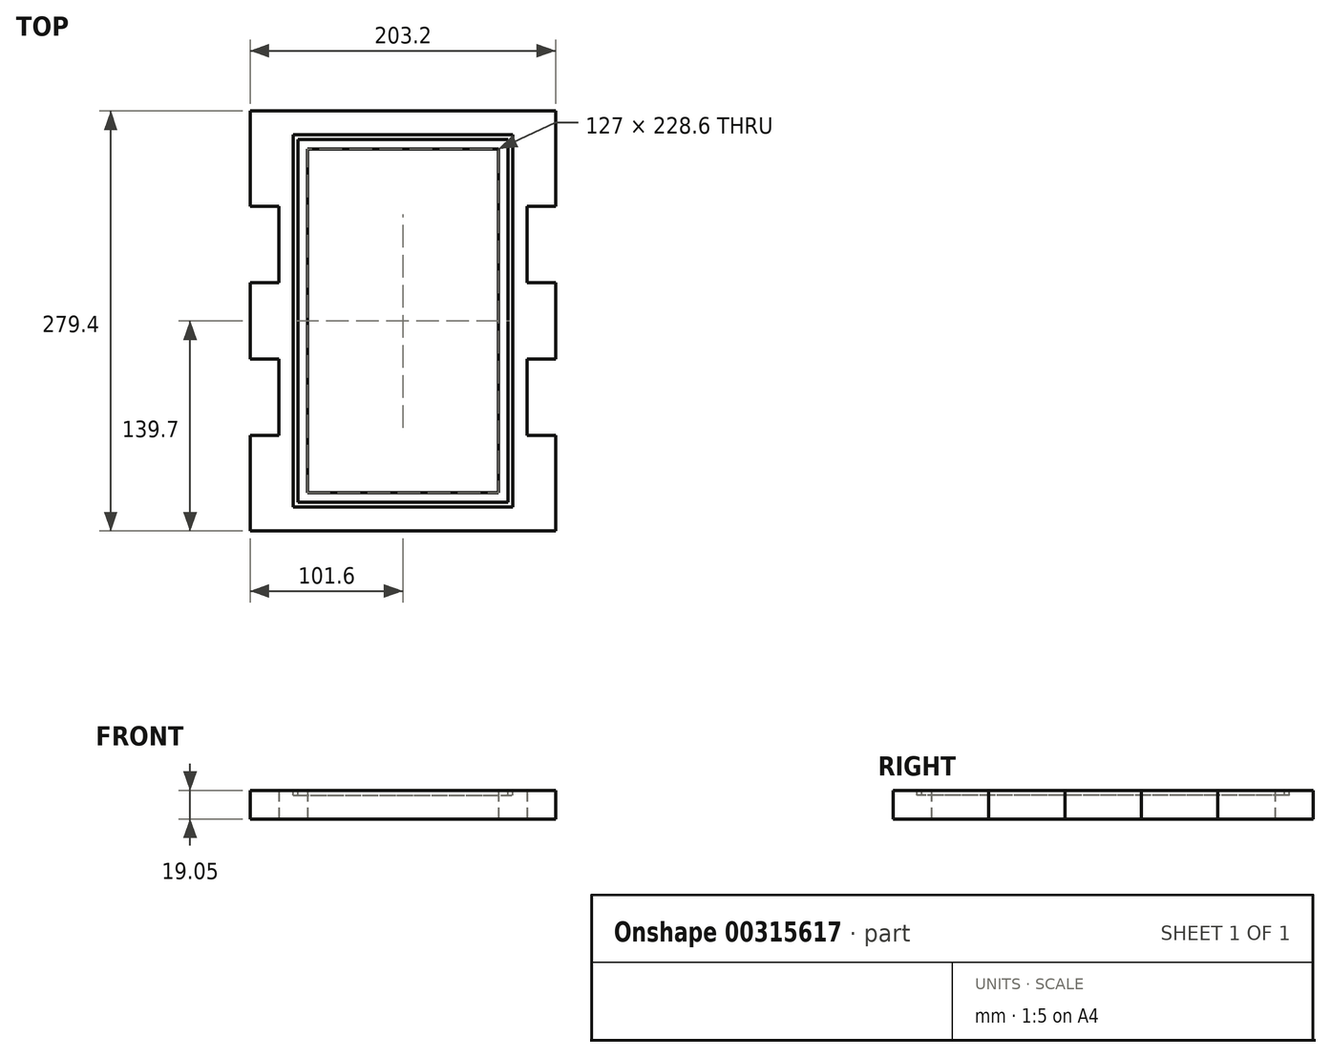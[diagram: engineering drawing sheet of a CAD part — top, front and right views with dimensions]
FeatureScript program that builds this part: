
annotation { "Feature Type Name" : "Feature", "Feature Type Description" : "" }
export const myFeature = defineFeature(function(context is Context, id is Id, definition is map)
    precondition{}
    {
        {
            var Q0;
            Q0=qCreatedBy(makeId("Top.planeOp"),FACE);
            var sketch = newSketch(context, id + "F0", { "sketchPlane" : qUnion([Q0])});
            skLineSegment(sketch, "E0.bottom", {"start": v(-101.6, 139.7) * mm, "end": v(101.6, 139.7) * mm});
            skLineSegment(sketch, "E0.top", {"start": v(-101.6, -139.7) * mm, "end": v(101.6, -139.7) * mm});
            skLineSegment(sketch, "E0.left", {"start": v(-101.6, 139.7) * mm, "end": v(-101.6, -139.7) * mm});
            skLineSegment(sketch, "E0.right", {"start": v(101.6, 139.7) * mm, "end": v(101.6, -139.7) * mm});
            skPoint(sketch, "E0.middle", {"position": v(0, 0) * mm});
            skLineSegment(sketch, "E1", {"start": v(-101.6, 76.2) * mm, "end": v(101.6, 76.2) * mm, "construction": true});
            skLineSegment(sketch, "E2", {"start": v(-101.6, -76.2) * mm, "end": v(101.6, -76.2) * mm, "construction": true});
            skLineSegment(sketch, "E3.bottom", {"start": v(-101.6, -76.2) * mm, "end": v(-82.55, -76.2) * mm});
            skLineSegment(sketch, "E3.top", {"start": v(-101.6, -25.4) * mm, "end": v(-82.55, -25.4) * mm});
            skLineSegment(sketch, "E3.left", {"start": v(-101.6, -76.2) * mm, "end": v(-101.6, -25.4) * mm});
            skLineSegment(sketch, "E3.right", {"start": v(-82.55, -76.2) * mm, "end": v(-82.55, -25.4) * mm});
            skLineSegment(sketch, "E4.bottom", {"start": v(-101.6, 76.2) * mm, "end": v(-82.55, 76.2) * mm});
            skLineSegment(sketch, "E4.top", {"start": v(-101.6, 25.4) * mm, "end": v(-82.55, 25.4) * mm});
            skLineSegment(sketch, "E4.left", {"start": v(-101.6, 76.2) * mm, "end": v(-101.6, 25.4) * mm});
            skLineSegment(sketch, "E4.right", {"start": v(-82.55, 76.2) * mm, "end": v(-82.55, 25.4) * mm});
            skLineSegment(sketch, "E5.bottom", {"start": v(101.6, 76.2) * mm, "end": v(82.55, 76.2) * mm});
            skLineSegment(sketch, "E5.top", {"start": v(101.6, 25.4) * mm, "end": v(82.55, 25.4) * mm});
            skLineSegment(sketch, "E5.left", {"start": v(101.6, 76.2) * mm, "end": v(101.6, 25.4) * mm});
            skLineSegment(sketch, "E5.right", {"start": v(82.55, 76.2) * mm, "end": v(82.55, 25.4) * mm});
            skLineSegment(sketch, "E6.bottom", {"start": v(101.6, -76.2) * mm, "end": v(82.55, -76.2) * mm});
            skLineSegment(sketch, "E6.top", {"start": v(101.6, -25.4) * mm, "end": v(82.55, -25.4) * mm});
            skLineSegment(sketch, "E6.left", {"start": v(101.6, -76.2) * mm, "end": v(101.6, -25.4) * mm});
            skLineSegment(sketch, "E6.right", {"start": v(82.55, -76.2) * mm, "end": v(82.55, -25.4) * mm});
            skLineSegment(sketch, "E7.bottom", {"start": v(-63.5, 114.3) * mm, "end": v(63.5, 114.3) * mm});
            skLineSegment(sketch, "E7.top", {"start": v(-63.5, -114.3) * mm, "end": v(63.5, -114.3) * mm});
            skLineSegment(sketch, "E7.left", {"start": v(-63.5, 114.3) * mm, "end": v(-63.5, -114.3) * mm});
            skLineSegment(sketch, "E7.right", {"start": v(63.5, 114.3) * mm, "end": v(63.5, -114.3) * mm});
            skSolve(sketch);
        }
        {
            var Q0;
            {var subQ10=sQuery(id+"F0.wireOp",EDGE,"E0.bottom");Q0=makeQuery(id+"F0.imprint","IMPRINT",FACE,{"disambiguationData":[TD([[makeQuery(id+"F0.imprint","IMPRINT",EDGE,{"derivedFrom":subQ10}),-1.0]])]});}
            extrude(context, id + "F1", {"entities" : qUnion([Q0]), "depth" : 19.05 * mm});
        }
        {
            var Q0;
            Q0=makeQuery(id+"F1.opExtrude","CAP_FACE",FACE,{"disambiguationData":[OSD([sQuery(id+"F0.wireOp",EDGE,"E0.bottom"),sQuery(id+"F0.wireOp",EDGE,"E0.top"),sQuery(id+"F0.wireOp",EDGE,"E0.left"),sQuery(id+"F0.wireOp",EDGE,"E0.right"),sQuery(id+"F0.wireOp",EDGE,"E3.bottom"),sQuery(id+"F0.wireOp",EDGE,"E3.top"),sQuery(id+"F0.wireOp",EDGE,"E3.right"),sQuery(id+"F0.wireOp",EDGE,"E4.bottom"),sQuery(id+"F0.wireOp",EDGE,"E4.top"),sQuery(id+"F0.wireOp",EDGE,"E4.right"),sQuery(id+"F0.wireOp",EDGE,"E5.bottom"),sQuery(id+"F0.wireOp",EDGE,"E5.top"),sQuery(id+"F0.wireOp",EDGE,"E5.right"),sQuery(id+"F0.wireOp",EDGE,"E6.bottom"),sQuery(id+"F0.wireOp",EDGE,"E6.top"),sQuery(id+"F0.wireOp",EDGE,"E6.right"),sQuery(id+"F0.wireOp",EDGE,"E7.bottom"),sQuery(id+"F0.wireOp",EDGE,"E7.top"),sQuery(id+"F0.wireOp",EDGE,"E7.left"),sQuery(id+"F0.wireOp",EDGE,"E7.right")])],"isStart":false});
            var sketch = newSketch(context, id + "F2", { "sketchPlane" : qUnion([Q0])});
            skLineSegment(sketch, "E8.bottom", {"start": v(-69.85, 120.65) * mm, "end": v(69.85, 120.65) * mm});
            skLineSegment(sketch, "E8.top", {"start": v(-69.85, -120.65) * mm, "end": v(69.85, -120.65) * mm});
            skLineSegment(sketch, "E8.left", {"start": v(-69.85, 120.65) * mm, "end": v(-69.85, -120.65) * mm});
            skLineSegment(sketch, "E8.right", {"start": v(69.85, 120.65) * mm, "end": v(69.85, -120.65) * mm});
            skPoint(sketch, "E8.middle", {"position": v(0, 0) * mm});
            skLineSegment(sketch, "E9.bottom", {"start": v(-73.02, 123.83) * mm, "end": v(73.02, 123.83) * mm});
            skLineSegment(sketch, "E9.top", {"start": v(-73.02, -123.83) * mm, "end": v(73.02, -123.83) * mm});
            skLineSegment(sketch, "E9.left", {"start": v(-73.03, 123.83) * mm, "end": v(-73.03, -123.83) * mm});
            skLineSegment(sketch, "E9.right", {"start": v(73.03, 123.83) * mm, "end": v(73.03, -123.83) * mm});
            skSolve(sketch);
        }
        {
            var Q0;
            Q0=makeQuery(id+"F2.imprint","IMPRINT",FACE,{"disambiguationData":[TD([[makeQuery(id+"F2.imprint","IMPRINT",EDGE,{"derivedFrom":sQuery(id+"F2.wireOp",EDGE,"E8.bottom")}),1.0]])]});
            extrude(context, id + "F3", {"entities" : qUnion([Q0]), "operationType" : NewBodyOperationType.REMOVE, "oppositeDirection" : true, "depth" : 3.17 * mm});
        }
    });
